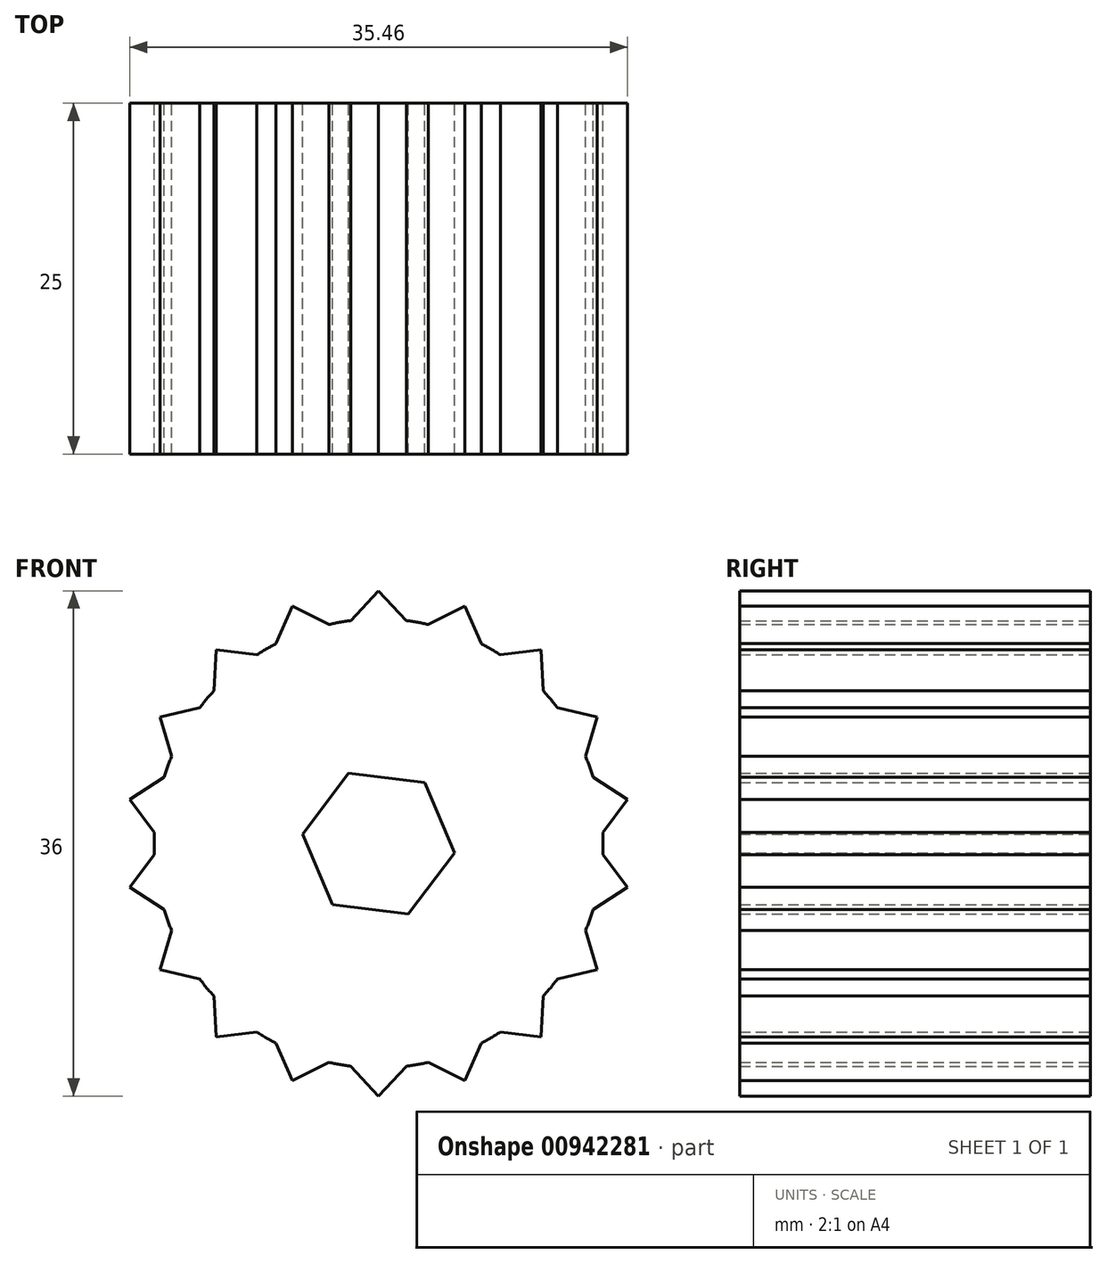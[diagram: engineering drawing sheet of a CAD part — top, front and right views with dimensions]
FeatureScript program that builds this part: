
annotation { "Feature Type Name" : "Feature", "Feature Type Description" : "" }
export const myFeature = defineFeature(function(context is Context, id is Id, definition is map)
    precondition{}
    {
        {
            var Q0;
            Q0=qCreatedBy(makeId("Front.planeOp"),FACE);
            var sketch = newSketch(context, id + "F0", { "sketchPlane" : qUnion([Q0])});
            skArc(sketch, "E0", {"start": v(-2, 15.88) * mm, "mid": v(-15.97, -1) * mm, "end": v(0, -16) * mm});
            skLineSegment(sketch, "E1", {"start": v(0, 18) * mm, "end": v(-2, 15.88) * mm});
            skLineSegment(sketch, "E2", {"start": v(0, 18) * mm, "end": v(2, 15.88) * mm});
            skPoint(sketch, "E3.center.orphan", {"position": v(0, 16) * mm});
            skArc(sketch, "E4", {"start": v(2, 15.88) * mm, "mid": v(0, 16) * mm, "end": v(-2, 15.88) * mm});
            skLineSegment(sketch, "E5.1.0", {"start": v(6.16, 16.91) * mm, "end": v(3.55, 15.6) * mm});
            skArc(sketch, "E5.1.1", {"start": v(7.3, 14.23) * mm, "mid": v(5.47, 15.04) * mm, "end": v(3.55, 15.6) * mm});
            skLineSegment(sketch, "E5.1.2", {"start": v(6.16, 16.91) * mm, "end": v(7.3, 14.23) * mm});
            skLineSegment(sketch, "E5.2.0", {"start": v(11.57, 13.79) * mm, "end": v(8.68, 13.44) * mm});
            skArc(sketch, "E5.2.1", {"start": v(11.73, 10.88) * mm, "mid": v(10.28, 12.26) * mm, "end": v(8.68, 13.44) * mm});
            skLineSegment(sketch, "E5.2.2", {"start": v(11.57, 13.79) * mm, "end": v(11.73, 10.88) * mm});
            skLineSegment(sketch, "E5.3.0", {"start": v(15.59, 9) * mm, "end": v(12.75, 9.67) * mm});
            skLineSegment(sketch, "E5.3.2", {"start": v(15.59, 9) * mm, "end": v(14.75, 6.2) * mm});
            skLineSegment(sketch, "E5.4.0", {"start": v(17.73, 3.13) * mm, "end": v(15.29, 4.72) * mm});
            skLineSegment(sketch, "E5.4.2", {"start": v(17.73, 3.13) * mm, "end": v(15.98, 0.8) * mm});
            skLineSegment(sketch, "E5.5.0", {"start": v(17.73, -3.13) * mm, "end": v(15.98, -0.8) * mm});
            skLineSegment(sketch, "E5.5.2", {"start": v(17.73, -3.13) * mm, "end": v(15.29, -4.72) * mm});
            skLineSegment(sketch, "E5.6.0", {"start": v(15.59, -9) * mm, "end": v(14.75, -6.2) * mm});
            skLineSegment(sketch, "E5.6.2", {"start": v(15.59, -9) * mm, "end": v(12.75, -9.67) * mm});
            skLineSegment(sketch, "E5.7.0", {"start": v(11.57, -13.79) * mm, "end": v(11.73, -10.88) * mm});
            skArc(sketch, "E5.7.1", {"start": v(8.68, -13.44) * mm, "mid": v(10.28, -12.26) * mm, "end": v(11.73, -10.88) * mm});
            skLineSegment(sketch, "E5.7.2", {"start": v(11.57, -13.79) * mm, "end": v(8.68, -13.44) * mm});
            skLineSegment(sketch, "E5.8.0", {"start": v(6.16, -16.91) * mm, "end": v(7.3, -14.23) * mm});
            skArc(sketch, "E5.8.1", {"start": v(3.55, -15.6) * mm, "mid": v(5.47, -15.04) * mm, "end": v(7.3, -14.23) * mm});
            skLineSegment(sketch, "E5.8.2", {"start": v(6.16, -16.91) * mm, "end": v(3.55, -15.6) * mm});
            skLineSegment(sketch, "E5.9.0", {"start": v(0, -18) * mm, "end": v(2, -15.88) * mm});
            skArc(sketch, "E5.9.1", {"start": v(0, -16) * mm, "mid": v(1, -15.97) * mm, "end": v(2, -15.88) * mm});
            skLineSegment(sketch, "E5.9.2", {"start": v(0, -18) * mm, "end": v(-2, -15.88) * mm});
            skLineSegment(sketch, "E6.1.1", {"start": v(-6.16, -16.91) * mm, "end": v(-7.3, -14.23) * mm});
            skLineSegment(sketch, "E6.1.2", {"start": v(-6.16, -16.91) * mm, "end": v(-3.55, -15.6) * mm});
            skLineSegment(sketch, "E6.2.1", {"start": v(-11.57, -13.79) * mm, "end": v(-11.73, -10.88) * mm});
            skLineSegment(sketch, "E6.2.2", {"start": v(-11.57, -13.79) * mm, "end": v(-8.68, -13.44) * mm});
            skLineSegment(sketch, "E6.3.1", {"start": v(-15.59, -9) * mm, "end": v(-14.75, -6.2) * mm});
            skLineSegment(sketch, "E6.3.2", {"start": v(-15.59, -9) * mm, "end": v(-12.75, -9.67) * mm});
            skLineSegment(sketch, "E6.4.1", {"start": v(-17.73, -3.13) * mm, "end": v(-15.98, -0.8) * mm});
            skLineSegment(sketch, "E6.4.2", {"start": v(-17.73, -3.13) * mm, "end": v(-15.29, -4.72) * mm});
            skLineSegment(sketch, "E6.5.1", {"start": v(-17.73, 3.13) * mm, "end": v(-15.29, 4.72) * mm});
            skLineSegment(sketch, "E6.5.2", {"start": v(-17.73, 3.13) * mm, "end": v(-15.98, 0.8) * mm});
            skLineSegment(sketch, "E6.6.1", {"start": v(-15.59, 9) * mm, "end": v(-12.75, 9.67) * mm});
            skLineSegment(sketch, "E6.6.2", {"start": v(-15.59, 9) * mm, "end": v(-14.75, 6.2) * mm});
            skLineSegment(sketch, "E6.7.1", {"start": v(-11.57, 13.79) * mm, "end": v(-8.68, 13.44) * mm});
            skLineSegment(sketch, "E6.7.2", {"start": v(-11.57, 13.79) * mm, "end": v(-11.73, 10.88) * mm});
            skLineSegment(sketch, "E6.8.1", {"start": v(-6.16, 16.91) * mm, "end": v(-3.55, 15.6) * mm});
            skLineSegment(sketch, "E6.8.2", {"start": v(-6.16, 16.91) * mm, "end": v(-7.3, 14.23) * mm});
            skPoint(sketch, "E7.orphan", {"position": v(2, 15.88) * mm});
            skPoint(sketch, "E8.orphan", {"position": v(-2, -15.88) * mm});
            skArc(sketch, "E9.trimOffspring", {"start": v(2, -15.88) * mm, "mid": v(2.78, -15.76) * mm, "end": v(3.55, -15.6) * mm});
            skArc(sketch, "E10.trimOffspring", {"start": v(7.3, -14.23) * mm, "mid": v(8, -13.86) * mm, "end": v(8.68, -13.44) * mm});
            skArc(sketch, "E11.trimOffspring", {"start": v(11.73, -10.88) * mm, "mid": v(16, 0) * mm, "end": v(11.73, 10.88) * mm});
            skArc(sketch, "E12.trimOffspring", {"start": v(8.68, 13.44) * mm, "mid": v(8, 13.86) * mm, "end": v(7.3, 14.23) * mm});
            skArc(sketch, "E13.trimOffspring", {"start": v(3.55, 15.6) * mm, "mid": v(2.78, 15.76) * mm, "end": v(2, 15.88) * mm});
            skCircle(sketch, "E14.cCircle", {"center": v(0, 0) * mm, "radius": 4.72 * mm, "construction": true});
            skLineSegment(sketch, "E14.0", {"start": v(3.28, 4.35) * mm, "end": v(5.4, -0.66) * mm});
            skLineSegment(sketch, "E14.1", {"start": v(5.4, -0.66) * mm, "end": v(2.13, -5.01) * mm});
            skLineSegment(sketch, "E14.2", {"start": v(2.13, -5.01) * mm, "end": v(-3.28, -4.35) * mm});
            skLineSegment(sketch, "E14.3", {"start": v(-3.28, -4.35) * mm, "end": v(-5.4, 0.66) * mm});
            skLineSegment(sketch, "E14.4", {"start": v(-5.4, 0.66) * mm, "end": v(-2.13, 5.01) * mm});
            skLineSegment(sketch, "E14.5", {"start": v(-2.13, 5.01) * mm, "end": v(3.28, 4.35) * mm});
            skPoint(sketch, "E14.0.midPoint", {"position": v(4.34, 1.84) * mm});
            skSolve(sketch);
        }
        {
            var Q0;
            {var subQ3=sQuery(id+"F0.wireOp",EDGE,"E4");Q0=makeQuery(id+"F0.imprint","IMPRINT",FACE,{"disambiguationData":[TD([[makeQuery(id+"F0.imprint","IMPRINT",EDGE,{"derivedFrom":subQ3}),1.0]])]});}
            var Q1;
            Q1=makeQuery(id+"F0.imprint","IMPRINT",FACE,{"disambiguationData":[TD([[makeQuery(id+"F0.imprint","IMPRINT",EDGE,{"derivedFrom":sQuery(id+"F0.wireOp",EDGE,"E5.1.0")}),1.0]])]});
            var Q2;
            Q2=makeQuery(id+"F0.imprint","IMPRINT",FACE,{"disambiguationData":[TD([[makeQuery(id+"F0.imprint","IMPRINT",EDGE,{"derivedFrom":sQuery(id+"F0.wireOp",EDGE,"E1")}),1.0]])]});
            var Q3;
            {var subQ0=sQuery(id+"F0.wireOp",EDGE,"E6.8.1");Q3=makeQuery(id+"F0.imprint","IMPRINT",FACE,{"disambiguationData":[TD([[makeQuery(id+"F0.imprint","IMPRINT",EDGE,{"derivedFrom":subQ0}),-1.0]])]});}
            var Q4;
            {var subQ0=sQuery(id+"F0.wireOp",EDGE,"E6.7.1");Q4=makeQuery(id+"F0.imprint","IMPRINT",FACE,{"disambiguationData":[TD([[makeQuery(id+"F0.imprint","IMPRINT",EDGE,{"derivedFrom":subQ0}),-1.0]])]});}
            var Q5;
            {var subQ0=sQuery(id+"F0.wireOp",EDGE,"E6.6.1");Q5=makeQuery(id+"F0.imprint","IMPRINT",FACE,{"disambiguationData":[TD([[makeQuery(id+"F0.imprint","IMPRINT",EDGE,{"derivedFrom":subQ0}),-1.0]])]});}
            var Q6;
            {var subQ0=sQuery(id+"F0.wireOp",EDGE,"E6.5.1");Q6=makeQuery(id+"F0.imprint","IMPRINT",FACE,{"disambiguationData":[TD([[makeQuery(id+"F0.imprint","IMPRINT",EDGE,{"derivedFrom":subQ0}),-1.0]])]});}
            var Q7;
            {var subQ0=sQuery(id+"F0.wireOp",EDGE,"E6.4.1");Q7=makeQuery(id+"F0.imprint","IMPRINT",FACE,{"disambiguationData":[TD([[makeQuery(id+"F0.imprint","IMPRINT",EDGE,{"derivedFrom":subQ0}),-1.0]])]});}
            var Q8;
            {var subQ0=sQuery(id+"F0.wireOp",EDGE,"E6.3.1");Q8=makeQuery(id+"F0.imprint","IMPRINT",FACE,{"disambiguationData":[TD([[makeQuery(id+"F0.imprint","IMPRINT",EDGE,{"derivedFrom":subQ0}),-1.0]])]});}
            var Q9;
            {var subQ0=sQuery(id+"F0.wireOp",EDGE,"E6.2.1");Q9=makeQuery(id+"F0.imprint","IMPRINT",FACE,{"disambiguationData":[TD([[makeQuery(id+"F0.imprint","IMPRINT",EDGE,{"derivedFrom":subQ0}),-1.0]])]});}
            var Q10;
            {var subQ0=sQuery(id+"F0.wireOp",EDGE,"E6.1.1");Q10=makeQuery(id+"F0.imprint","IMPRINT",FACE,{"disambiguationData":[TD([[makeQuery(id+"F0.imprint","IMPRINT",EDGE,{"derivedFrom":subQ0}),-1.0]])]});}
            var Q11;
            Q11=makeQuery(id+"F0.imprint","IMPRINT",FACE,{"disambiguationData":[TD([[makeQuery(id+"F0.imprint","IMPRINT",EDGE,{"derivedFrom":sQuery(id+"F0.wireOp",EDGE,"E5.9.0")}),1.0]])]});
            var Q12;
            Q12=makeQuery(id+"F0.imprint","IMPRINT",FACE,{"disambiguationData":[TD([[makeQuery(id+"F0.imprint","IMPRINT",EDGE,{"derivedFrom":sQuery(id+"F0.wireOp",EDGE,"E5.8.0")}),1.0]])]});
            var Q13;
            {var subQ0=sQuery(id+"F0.wireOp",EDGE,"E5.6.0");Q13=makeQuery(id+"F0.imprint","IMPRINT",FACE,{"disambiguationData":[TD([[makeQuery(id+"F0.imprint","IMPRINT",EDGE,{"derivedFrom":subQ0}),1.0]])]});}
            var Q14;
            {var subQ0=sQuery(id+"F0.wireOp",EDGE,"E5.5.0");Q14=makeQuery(id+"F0.imprint","IMPRINT",FACE,{"disambiguationData":[TD([[makeQuery(id+"F0.imprint","IMPRINT",EDGE,{"derivedFrom":subQ0}),1.0]])]});}
            var Q15;
            {var subQ0=sQuery(id+"F0.wireOp",EDGE,"E5.4.0");Q15=makeQuery(id+"F0.imprint","IMPRINT",FACE,{"disambiguationData":[TD([[makeQuery(id+"F0.imprint","IMPRINT",EDGE,{"derivedFrom":subQ0}),1.0]])]});}
            var Q16;
            {var subQ0=sQuery(id+"F0.wireOp",EDGE,"E5.3.0");Q16=makeQuery(id+"F0.imprint","IMPRINT",FACE,{"disambiguationData":[TD([[makeQuery(id+"F0.imprint","IMPRINT",EDGE,{"derivedFrom":subQ0}),1.0]])]});}
            var Q17;
            Q17=makeQuery(id+"F0.imprint","IMPRINT",FACE,{"disambiguationData":[TD([[makeQuery(id+"F0.imprint","IMPRINT",EDGE,{"derivedFrom":sQuery(id+"F0.wireOp",EDGE,"E5.2.0")}),1.0]])]});
            var Q18;
            Q18=makeQuery(id+"F0.imprint","IMPRINT",FACE,{"disambiguationData":[TD([[makeQuery(id+"F0.imprint","IMPRINT",EDGE,{"derivedFrom":sQuery(id+"F0.wireOp",EDGE,"E5.7.0")}),1.0]])]});
            extrude(context, id + "F1", {"entities" : qUnion([Q0, Q1, Q2, Q3, Q4, Q5, Q6, Q7, Q8, Q9, Q10, Q11, Q12, Q13, Q14, Q15, Q16, Q17, Q18]), "depth" : 25 * mm, "offsetDistance" : 25 * mm});
        }
    });
